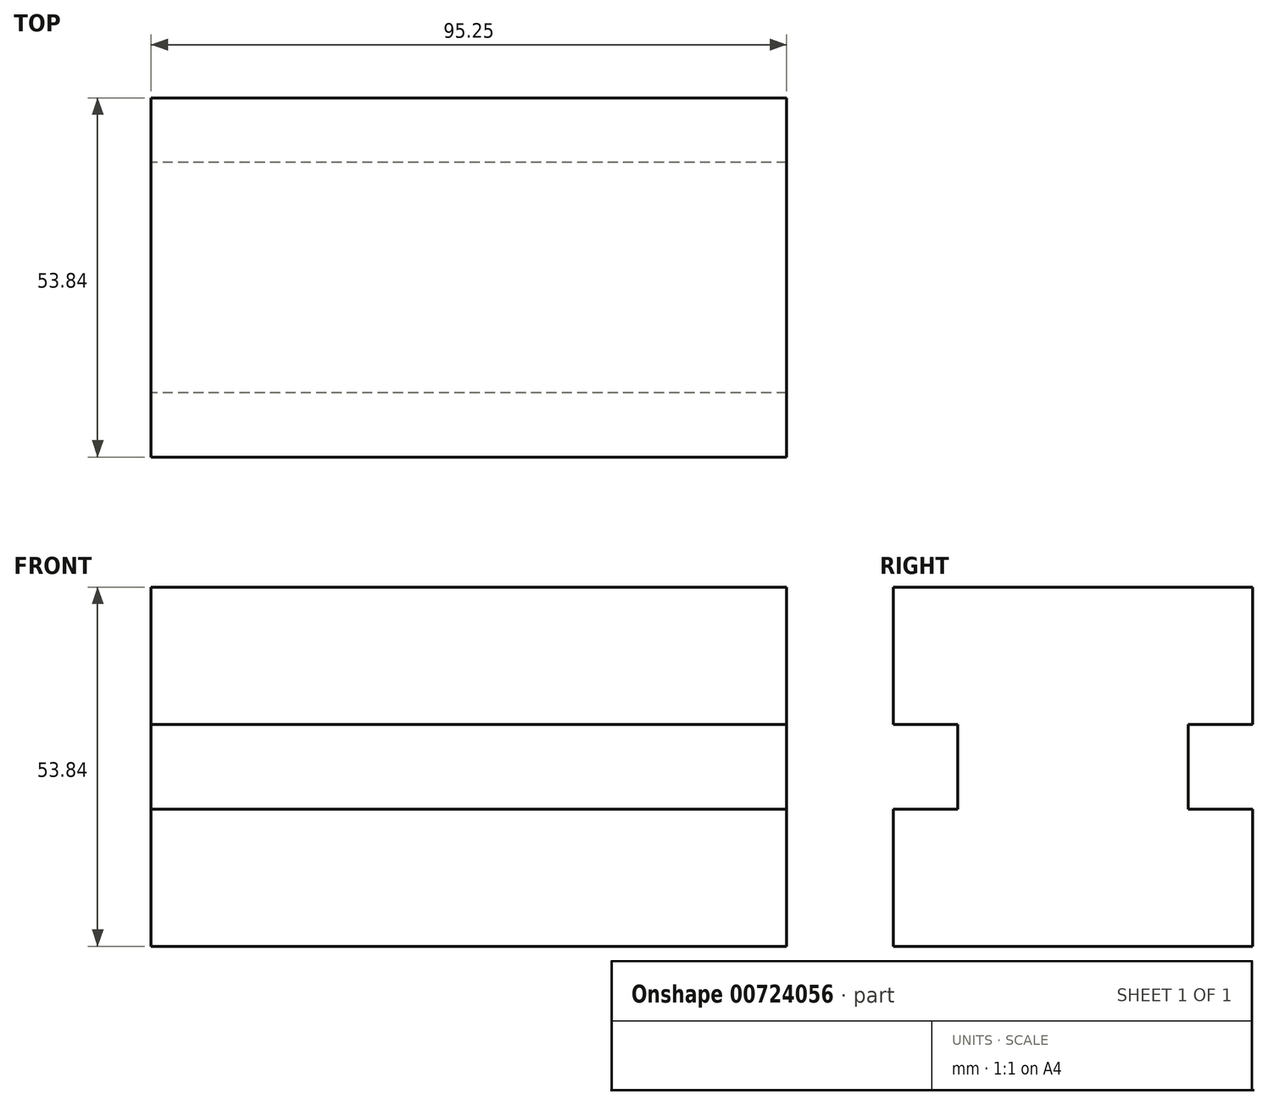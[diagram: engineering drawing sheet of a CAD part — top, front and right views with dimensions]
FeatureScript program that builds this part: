
annotation { "Feature Type Name" : "Feature", "Feature Type Description" : "" }
export const myFeature = defineFeature(function(context is Context, id is Id, definition is map)
    precondition{}
    {
        {
            var Q0;
            Q0=qCreatedBy(makeId("Right.planeOp"),FACE);
            var sketch = newSketch(context, id + "F0", { "sketchPlane" : qUnion([Q0])});
            skLineSegment(sketch, "E0.bottom", {"start": v(26.92, 26.92) * mm, "end": v(-26.92, 26.92) * mm});
            skLineSegment(sketch, "E0.top", {"start": v(26.92, -26.92) * mm, "end": v(-26.92, -26.92) * mm});
            skLineSegment(sketch, "E0.left", {"start": v(26.92, 26.92) * mm, "end": v(26.92, 6.35) * mm});
            skPoint(sketch, "E0.middle", {"position": v(0, 0) * mm});
            skLineSegment(sketch, "E1.bottom", {"start": v(-26.92, 6.35) * mm, "end": v(-17.27, 6.35) * mm});
            skLineSegment(sketch, "E1.top", {"start": v(-26.92, -6.35) * mm, "end": v(-17.27, -6.35) * mm});
            skLineSegment(sketch, "E1.right", {"start": v(-17.27, 6.35) * mm, "end": v(-17.27, -6.35) * mm});
            skLineSegment(sketch, "E2.trimOffspring", {"start": v(-26.92, -6.35) * mm, "end": v(-26.92, -26.92) * mm});
            skLineSegment(sketch, "E3", {"start": v(-26.92, 26.92) * mm, "end": v(-26.92, 6.35) * mm});
            skLineSegment(sketch, "E4", {"start": v(0, 31.3) * mm, "end": v(0, -30.46) * mm, "construction": true});
            skLineSegment(sketch, "E5.MirrorCS", {"start": v(26.92, 6.35) * mm, "end": v(17.27, 6.35) * mm});
            skLineSegment(sketch, "E6.MirrorCS", {"start": v(17.27, 6.35) * mm, "end": v(17.27, -6.35) * mm});
            skLineSegment(sketch, "E7.MirrorCS", {"start": v(26.92, -6.35) * mm, "end": v(17.27, -6.35) * mm});
            skLineSegment(sketch, "E8.trimOffspring", {"start": v(26.92, -6.35) * mm, "end": v(26.92, -26.92) * mm});
            skSolve(sketch);
        }
        {
            var Q0;
            Q0=makeQuery(id+"F0.imprint","IMPRINT",FACE,{"disambiguationData":[TD([[makeQuery(id+"F0.imprint","IMPRINT",EDGE,{"derivedFrom":sQuery(id+"F0.wireOp",EDGE,"E0.bottom")}),1.0]])]});
            extrude(context, id + "F1", {"entities" : qUnion([Q0]), "depth" : 95.25 * mm, "offsetDistance" : 25.4 * mm});
        }
    });
